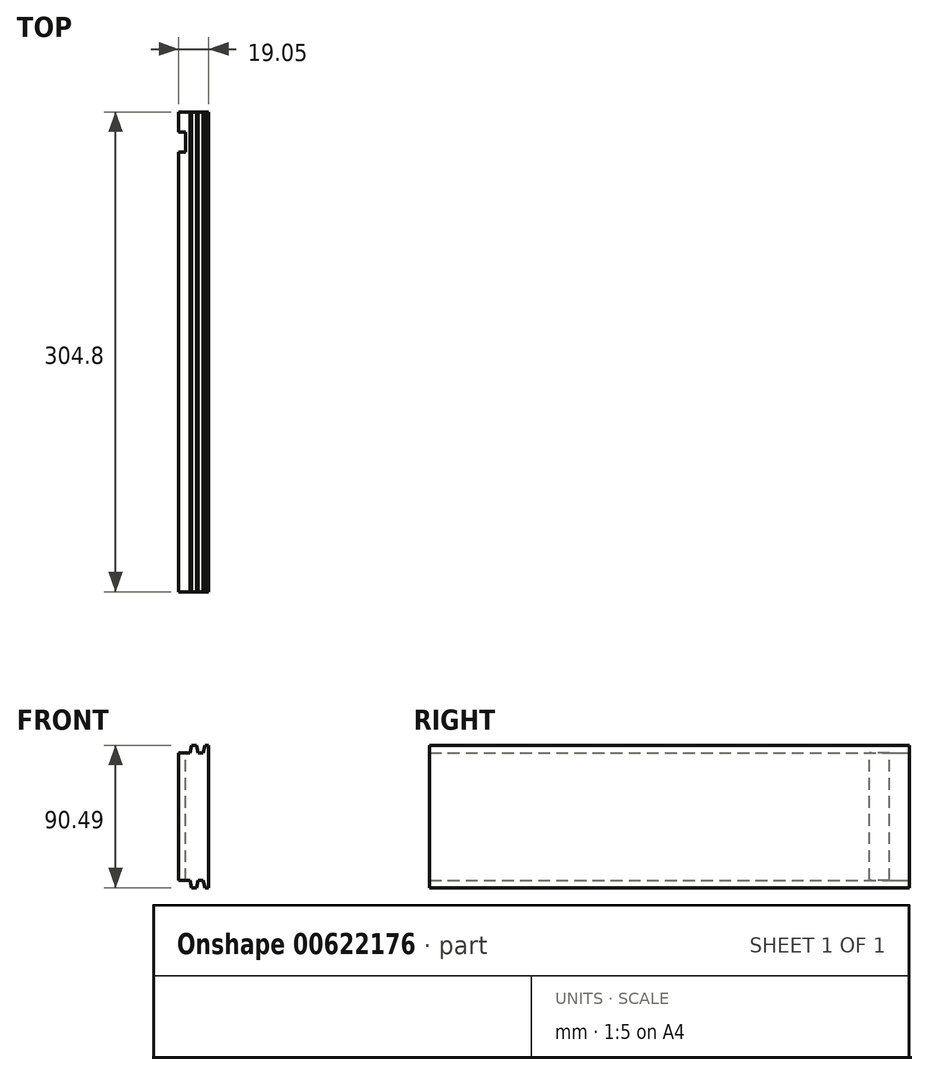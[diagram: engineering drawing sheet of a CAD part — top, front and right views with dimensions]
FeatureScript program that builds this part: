
annotation { "Feature Type Name" : "Feature", "Feature Type Description" : "" }
export const myFeature = defineFeature(function(context is Context, id is Id, definition is map)
    precondition{}
    {
        {
            var Q0;
            Q0=qCreatedBy(makeId("Front.planeOp"),FACE);
            var sketch = newSketch(context, id + "F0", { "sketchPlane" : qUnion([Q0])});
            skLineSegment(sketch, "E0.bottom", {"start": v(0, 0) * mm, "end": v(19.05, 0) * mm});
            skLineSegment(sketch, "E0.top", {"start": v(0, 90.49) * mm, "end": v(19.05, 90.49) * mm});
            skLineSegment(sketch, "E0.left", {"start": v(0, 0) * mm, "end": v(0, 90.49) * mm});
            skLineSegment(sketch, "E0.right", {"start": v(19.05, 0) * mm, "end": v(19.05, 90.49) * mm});
            skSolve(sketch);
        }
        {
            var Q0;
            Q0 = qSketchRegion(id + "F0", true);
            extrude(context, id + "F1", {"entities" : qUnion([Q0]), "depth" : 304.8 * mm, "offsetDistance" : 25.4 * mm});
        }
        {
            var Q0;
            Q0=qCreatedBy(makeId("Front.planeOp"),FACE);
            cPlane(context, id + "F2", {"entities" : qUnion([Q0]), "cplaneType" : CPlaneType.OFFSET, "offset" : 25.4 * mm, "width" : 152.4 * mm, "height" : 152.4 * mm});
        }
        {
            var Q0;
            Q0=qCreatedBy(id+"F2.planeOp",FACE);
            var sketch = newSketch(context, id + "F3", { "sketchPlane" : qUnion([Q0])});
            skLineSegment(sketch, "E1.bottom", {"start": v(-8.2, 0) * mm, "end": v(4.5, 0) * mm});
            skLineSegment(sketch, "E1.top", {"start": v(-8.2, 101.6) * mm, "end": v(4.5, 101.6) * mm});
            skLineSegment(sketch, "E1.left", {"start": v(-8.2, 0) * mm, "end": v(-8.2, 101.6) * mm});
            skLineSegment(sketch, "E1.right", {"start": v(4.5, 0) * mm, "end": v(4.5, 101.6) * mm});
            skSolve(sketch);
        }
        {
            var Q0;
            Q0 = qSketchRegion(id + "F3", true);
            extrude(context, id + "F4", {"entities" : qUnion([Q0]), "operationType" : NewBodyOperationType.REMOVE, "oppositeDirection" : true, "depth" : 12.7 * mm, "offsetDistance" : 25.4 * mm});
        }
        {
            var Q0;
            Q0=qCreatedBy(makeId("Front.planeOp"),FACE);
            var sketch = newSketch(context, id + "F5", { "sketchPlane" : qUnion([Q0])});
            skLineSegment(sketch, "E2", {"start": v(26.19, -5.09) * mm, "end": v(-2.39, -5.09) * mm});
            skLineSegment(sketch, "E3", {"start": v(-2.39, -5.09) * mm, "end": v(-2.39, 4.76) * mm});
            skLineSegment(sketch, "E4", {"start": v(-2.39, 4.76) * mm, "end": v(7.14, 4.76) * mm});
            skLineSegment(sketch, "E5", {"start": v(7.14, 4.76) * mm, "end": v(8.2, 0) * mm});
            skLineSegment(sketch, "E6", {"start": v(8.2, 0) * mm, "end": v(11.37, 0) * mm});
            skLineSegment(sketch, "E7", {"start": v(11.37, 0) * mm, "end": v(12.43, 4.76) * mm});
            skLineSegment(sketch, "E8", {"start": v(12.43, 4.76) * mm, "end": v(15.6, 4.76) * mm});
            skLineSegment(sketch, "E9", {"start": v(15.6, 4.76) * mm, "end": v(16.66, 0) * mm});
            skLineSegment(sketch, "E10", {"start": v(16.66, 0) * mm, "end": v(26.19, 0) * mm});
            skLineSegment(sketch, "E11", {"start": v(26.19, 0) * mm, "end": v(26.19, -5.09) * mm});
            skPoint(sketch, "E12.positionSnap0", {"position": v(11.9, -5.09) * mm});
            skPoint(sketch, "E13", {"position": v(8.2, 0) * mm});
            skSolve(sketch);
        }
        {
            var Q0;
            Q0 = qSketchRegion(id + "F5", true);
            extrude(context, id + "F6", {"entities" : qUnion([Q0]), "operationType" : NewBodyOperationType.REMOVE, "depth" : 304.8 * mm, "offsetDistance" : 25.4 * mm});
        }
        {
            var Q0;
            Q0=qCreatedBy(makeId("Front.planeOp"),FACE);
            var sketch = newSketch(context, id + "F7", { "sketchPlane" : qUnion([Q0])});
            skLineSegment(sketch, "E14", {"start": v(26.19, 95.58) * mm, "end": v(-2.39, 95.58) * mm});
            skLineSegment(sketch, "E15.MirrorCS", {"start": v(12.43, 85.73) * mm, "end": v(15.6, 85.73) * mm});
            skLineSegment(sketch, "E16.MirrorCS", {"start": v(26.19, 90.49) * mm, "end": v(26.19, 95.58) * mm});
            skLineSegment(sketch, "E17.MirrorCS", {"start": v(8.2, 90.49) * mm, "end": v(11.37, 90.49) * mm});
            skLineSegment(sketch, "E18.MirrorCS", {"start": v(15.6, 85.73) * mm, "end": v(16.66, 90.49) * mm});
            skLineSegment(sketch, "E19.MirrorCS", {"start": v(16.66, 90.49) * mm, "end": v(26.19, 90.49) * mm});
            skLineSegment(sketch, "E20.MirrorCS", {"start": v(11.37, 90.49) * mm, "end": v(12.43, 85.72) * mm});
            skLineSegment(sketch, "E21.MirrorCS", {"start": v(7.14, 85.73) * mm, "end": v(8.2, 90.49) * mm});
            skLineSegment(sketch, "E22.MirrorCS", {"start": v(-2.39, 85.73) * mm, "end": v(7.14, 85.73) * mm});
            skLineSegment(sketch, "E23.MirrorCS", {"start": v(-2.39, 95.58) * mm, "end": v(-2.39, 85.73) * mm});
            skLineSegment(sketch, "E24", {"start": v(-2.39, 95.58) * mm, "end": v(26.19, 95.58) * mm});
            skPoint(sketch, "E25", {"position": v(11.9, 95.58) * mm});
            skPoint(sketch, "E26", {"position": v(8.2, 90.49) * mm});
            skSolve(sketch);
        }
        {
            var Q0;
            Q0 = qSketchRegion(id + "F7", true);
            extrude(context, id + "F8", {"entities" : qUnion([Q0]), "operationType" : NewBodyOperationType.REMOVE, "depth" : 304.8 * mm, "offsetDistance" : 25.4 * mm});
        }
    });
